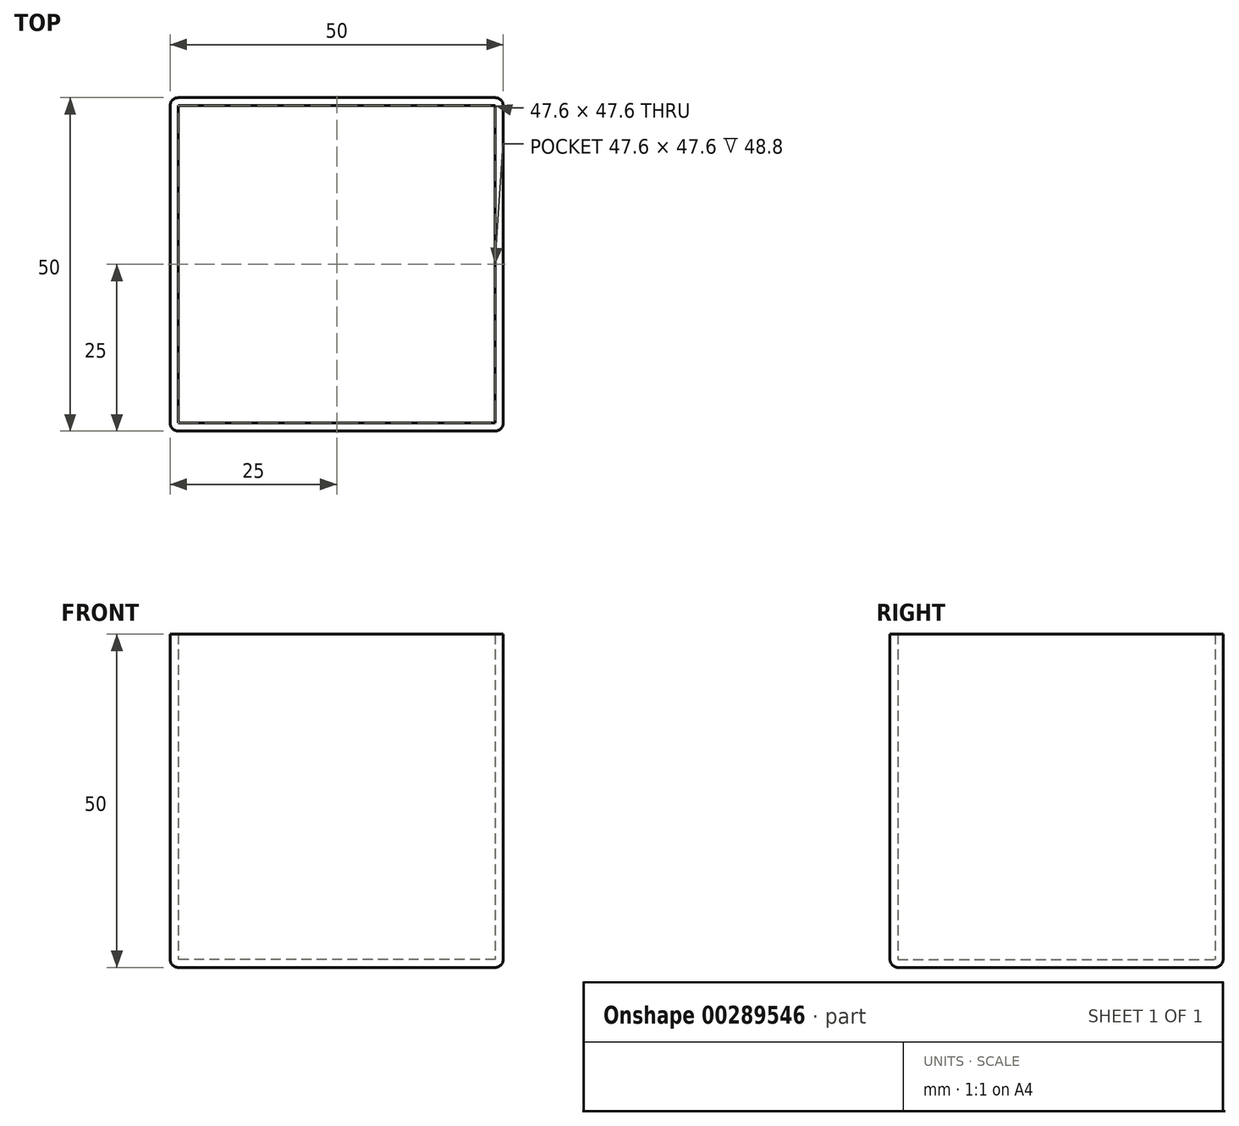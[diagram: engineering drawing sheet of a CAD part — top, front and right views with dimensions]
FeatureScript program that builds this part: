
annotation { "Feature Type Name" : "Feature", "Feature Type Description" : "" }
export const myFeature = defineFeature(function(context is Context, id is Id, definition is map)
    precondition{}
    {
        {
            var Q0;
            Q0=qCreatedBy(makeId("Top.planeOp"),FACE);
            var sketch = newSketch(context, id + "F0", { "sketchPlane" : qUnion([Q0])});
            skLineSegment(sketch, "E0.bottom", {"start": v(0, 0) * mm, "end": v(-50, 0) * mm});
            skLineSegment(sketch, "E0.top", {"start": v(0, 50) * mm, "end": v(-50, 50) * mm});
            skLineSegment(sketch, "E0.left", {"start": v(0, 0) * mm, "end": v(0, 50) * mm});
            skLineSegment(sketch, "E0.right", {"start": v(-50, 0) * mm, "end": v(-50, 50) * mm});
            skSolve(sketch);
        }
        {
            var Q0;
            Q0=makeQuery(id+"F0.imprint","IMPRINT",FACE,{"disambiguationData":[TD([[makeQuery(id+"F0.imprint","IMPRINT",EDGE,{"derivedFrom":sQuery(id+"F0.wireOp",EDGE,"E0.bottom")}),-1.0]])]});
            extrude(context, id + "F1", {"entities" : qUnion([Q0]), "depth" : 50 * mm});
        }
        {
            var Q0;
            Q0=makeQuery(id+"F1.opExtrude","CAP_FACE",FACE,{"disambiguationData":[OSD([sQuery(id+"F0.wireOp",EDGE,"E0.bottom"),sQuery(id+"F0.wireOp",EDGE,"E0.top"),sQuery(id+"F0.wireOp",EDGE,"E0.left"),sQuery(id+"F0.wireOp",EDGE,"E0.right")])],"isStart":false});
            shell(context, id + "F2", {"entities" : qUnion([Q0]), "thickness" : 1.2 * mm});
        }
        {
            var Q0;
            Q0=makeQuery(id+"F1.opExtrude","SWEPT_EDGE",EDGE,{"disambiguationData":[OSD([sQuery(id+"F0.wireOp",EDGE,"E0.top"),sQuery(id+"F0.wireOp",EDGE,"E0.right")])]});
            var Q1;
            Q1=makeQuery(id+"F1.opExtrude","SWEPT_EDGE",EDGE,{"disambiguationData":[OSD([sQuery(id+"F0.wireOp",EDGE,"E0.bottom"),sQuery(id+"F0.wireOp",EDGE,"E0.right")])]});
            var Q2;
            Q2=makeQuery(id+"F1.opExtrude","SWEPT_EDGE",EDGE,{"disambiguationData":[OSD([sQuery(id+"F0.wireOp",EDGE,"E0.bottom"),sQuery(id+"F0.wireOp",EDGE,"E0.left")])]});
            var Q3;
            Q3=makeQuery(id+"F1.opExtrude","SWEPT_EDGE",EDGE,{"disambiguationData":[OSD([sQuery(id+"F0.wireOp",EDGE,"E0.top"),sQuery(id+"F0.wireOp",EDGE,"E0.left")])]});
            fillet(context, id + "F3", {"entities" : qUnion([Q0, Q1, Q2, Q3]), "radius" : 1.2 * mm, "tangentPropagation" : true, "allowEdgeOverflow" : false});
        }
        {
            var Q0;
            Q0=makeQuery(id+"F1.opExtrude","CAP_EDGE",EDGE,{"disambiguationData":[OSD([sQuery(id+"F0.wireOp",EDGE,"E0.top")])],"isStart":true});
            var Q1;
            Q1=makeQuery(id+"F1.opExtrude","CAP_EDGE",EDGE,{"disambiguationData":[OSD([sQuery(id+"F0.wireOp",EDGE,"E0.right")])],"isStart":true});
            var Q2;
            Q2=makeQuery(id+"F1.opExtrude","CAP_EDGE",EDGE,{"disambiguationData":[OSD([sQuery(id+"F0.wireOp",EDGE,"E0.left")])],"isStart":true});
            var Q3;
            Q3=makeQuery(id+"F1.opExtrude","CAP_EDGE",EDGE,{"disambiguationData":[OSD([sQuery(id+"F0.wireOp",EDGE,"E0.bottom")])],"isStart":true});
            fillet(context, id + "F4", {"entities" : qUnion([Q0, Q1, Q2, Q3]), "radius" : 1.2 * mm, "tangentPropagation" : true, "allowEdgeOverflow" : false});
        }
    });
